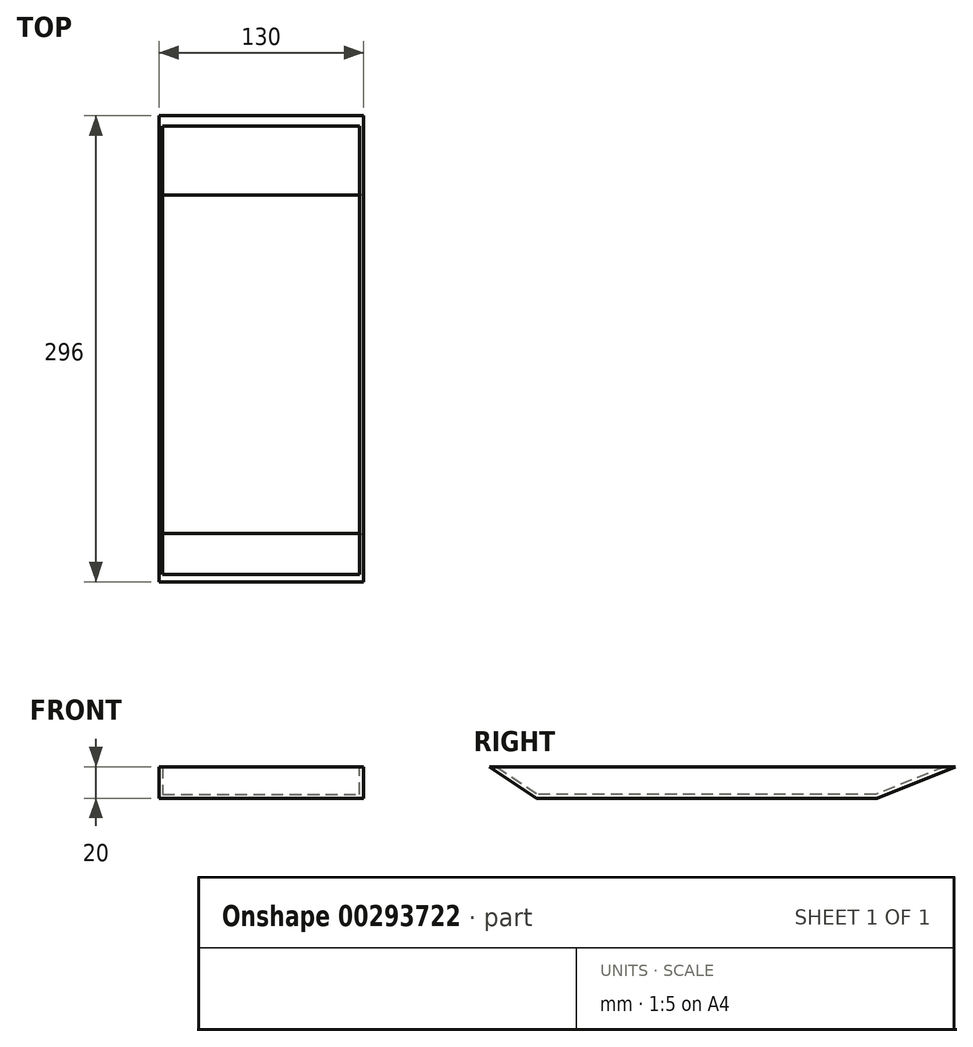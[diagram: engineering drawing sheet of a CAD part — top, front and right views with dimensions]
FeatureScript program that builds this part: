
annotation { "Feature Type Name" : "Feature", "Feature Type Description" : "" }
export const myFeature = defineFeature(function(context is Context, id is Id, definition is map)
    precondition{}
    {
        {
            var Q0;
            Q0=qCreatedBy(makeId("Top.planeOp"),FACE);
            var sketch = newSketch(context, id + "F0", { "sketchPlane" : qUnion([Q0])});
            skLineSegment(sketch, "E0.bottom", {"start": v(-65, 148) * mm, "end": v(65, 148) * mm});
            skLineSegment(sketch, "E0.top", {"start": v(-65, -148) * mm, "end": v(65, -148) * mm});
            skLineSegment(sketch, "E0.left", {"start": v(-65, 148) * mm, "end": v(-65, -148) * mm});
            skLineSegment(sketch, "E0.right", {"start": v(65, 148) * mm, "end": v(65, -148) * mm});
            skPoint(sketch, "E0.middle", {"position": v(0, 0) * mm});
            skSolve(sketch);
        }
        {
            var Q0;
            Q0 = qSketchRegion(id + "F0", true);
            extrude(context, id + "F1", {"entities" : qUnion([Q0]), "endBound" : BoundingType.SYMMETRIC, "depth" : 20 * mm});
        }
        {
            var Q0;
            Q0=makeQuery(id+"F1.opExtrude","CAP_EDGE",EDGE,{"disambiguationData":[OSD([sQuery(id+"F0.wireOp",EDGE,"E0.top")])],"isStart":true});
            chamfer(context, id + "F2", {"entities" : qUnion([Q0]), "chamferType" : ChamferType.TWO_OFFSETS, "width1" : 20 * mm, "oppositeDirection" : false, "width2" : 30 * mm, "tangentPropagation" : true});
        }
        {
            var Q0;
            Q0=makeQuery(id+"F1.opExtrude","CAP_EDGE",EDGE,{"disambiguationData":[OSD([sQuery(id+"F0.wireOp",EDGE,"E0.bottom")])],"isStart":true});
            chamfer(context, id + "F3", {"entities" : qUnion([Q0]), "chamferType" : ChamferType.TWO_OFFSETS, "width1" : 50 * mm, "oppositeDirection" : false, "width2" : 20 * mm, "tangentPropagation" : true});
        }
        {
            var Q0;
            Q0=makeQuery(id+"F1.opExtrude","CAP_FACE",FACE,{"disambiguationData":[OSD([sQuery(id+"F0.wireOp",EDGE,"E0.bottom"),sQuery(id+"F0.wireOp",EDGE,"E0.top"),sQuery(id+"F0.wireOp",EDGE,"E0.left"),sQuery(id+"F0.wireOp",EDGE,"E0.right")])],"isStart":false});
            shell(context, id + "F4", {"entities" : qUnion([Q0]), "thickness" : 2.5 * mm});
        }
    });
